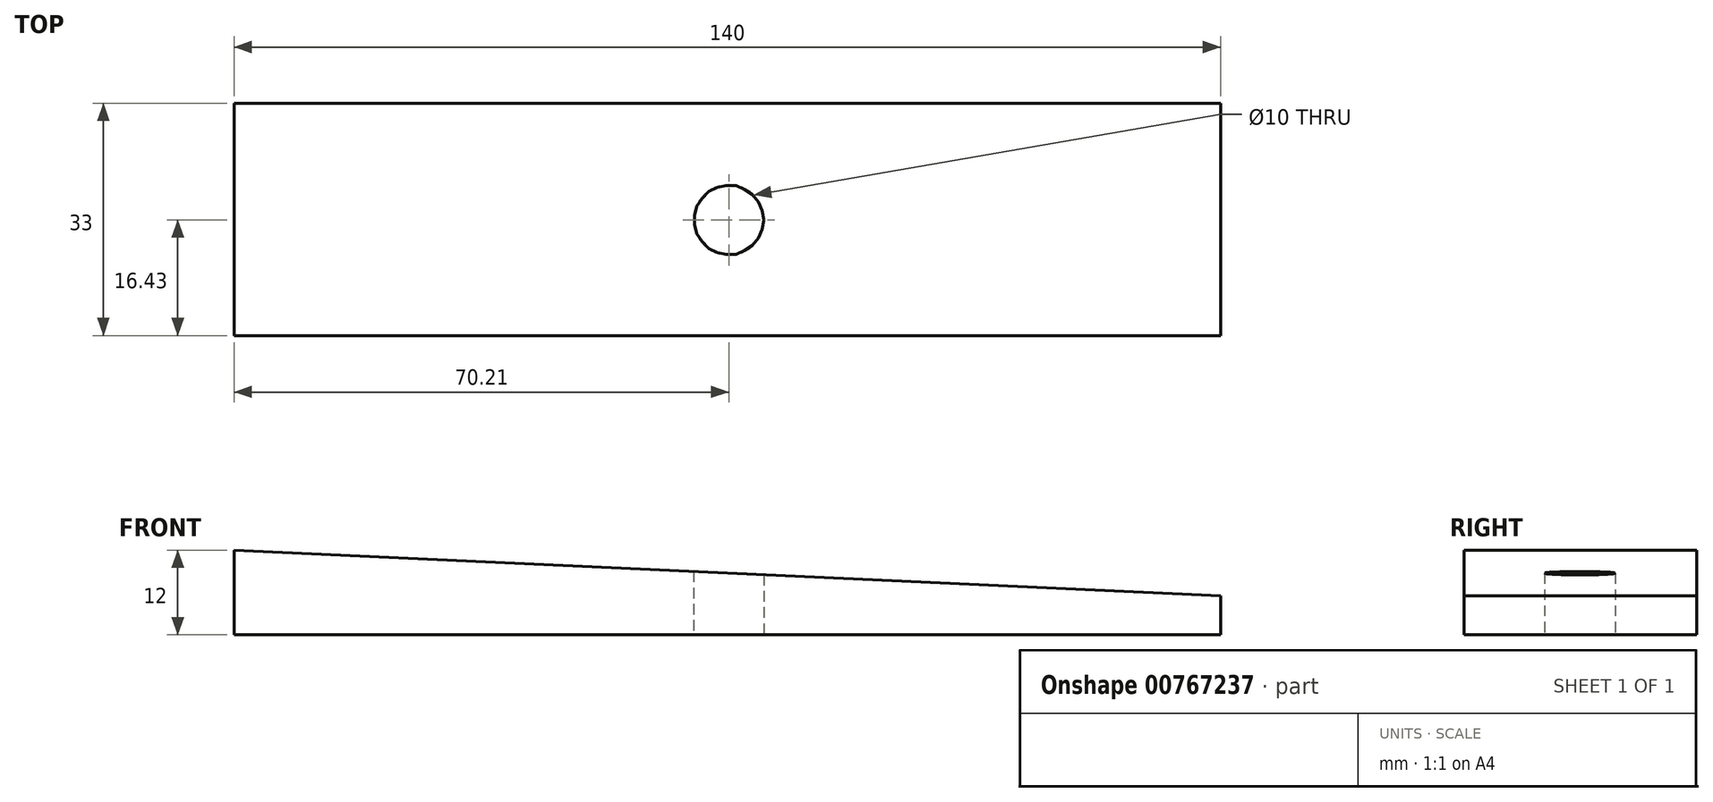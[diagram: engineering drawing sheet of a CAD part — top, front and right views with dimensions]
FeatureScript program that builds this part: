
annotation { "Feature Type Name" : "Feature", "Feature Type Description" : "" }
export const myFeature = defineFeature(function(context is Context, id is Id, definition is map)
    precondition{}
    {
        {
            var Q0;
            Q0=qCreatedBy(makeId("Top.planeOp"),FACE);
            var sketch = newSketch(context, id + "F0", { "sketchPlane" : qUnion([Q0])});
            skLineSegment(sketch, "E0.bottom", {"start": v(-70.21, 16.57) * mm, "end": v(69.79, 16.57) * mm});
            skLineSegment(sketch, "E0.top", {"start": v(-70.21, -16.43) * mm, "end": v(69.79, -16.43) * mm});
            skLineSegment(sketch, "E0.left", {"start": v(-70.21, 16.57) * mm, "end": v(-70.21, -16.43) * mm});
            skLineSegment(sketch, "E0.right", {"start": v(69.79, 16.57) * mm, "end": v(69.79, -16.43) * mm});
            skCircle(sketch, "E1", {"center": v(0, 0) * mm, "radius": 5 * mm});
            skSolve(sketch);
        }
        {
            var Q0;
            Q0=makeQuery(id+"F0.imprint","IMPRINT",FACE,{"disambiguationData":[TD([[makeQuery(id+"F0.imprint","IMPRINT",EDGE,{"derivedFrom":sQuery(id+"F0.wireOp",EDGE,"E0.bottom")}),-1.0]])]});
            extrude(context, id + "F1", {"entities" : qUnion([Q0]), "depth" : 12 * mm, "offsetDistance" : 25 * mm});
        }
        {
            var Q0;
            Q0=makeQuery(id+"F1.opExtrude","CAP_EDGE",EDGE,{"disambiguationData":[OSD([sQuery(id+"F0.wireOp",EDGE,"E0.right")])],"isStart":false});
            chamfer(context, id + "F2", {"entities" : qUnion([Q0]), "chamferType" : ChamferType.TWO_OFFSETS, "width1" : 6.5 * mm, "oppositeDirection" : false, "width2" : 140 * mm, "tangentPropagation" : true});
        }
    });
